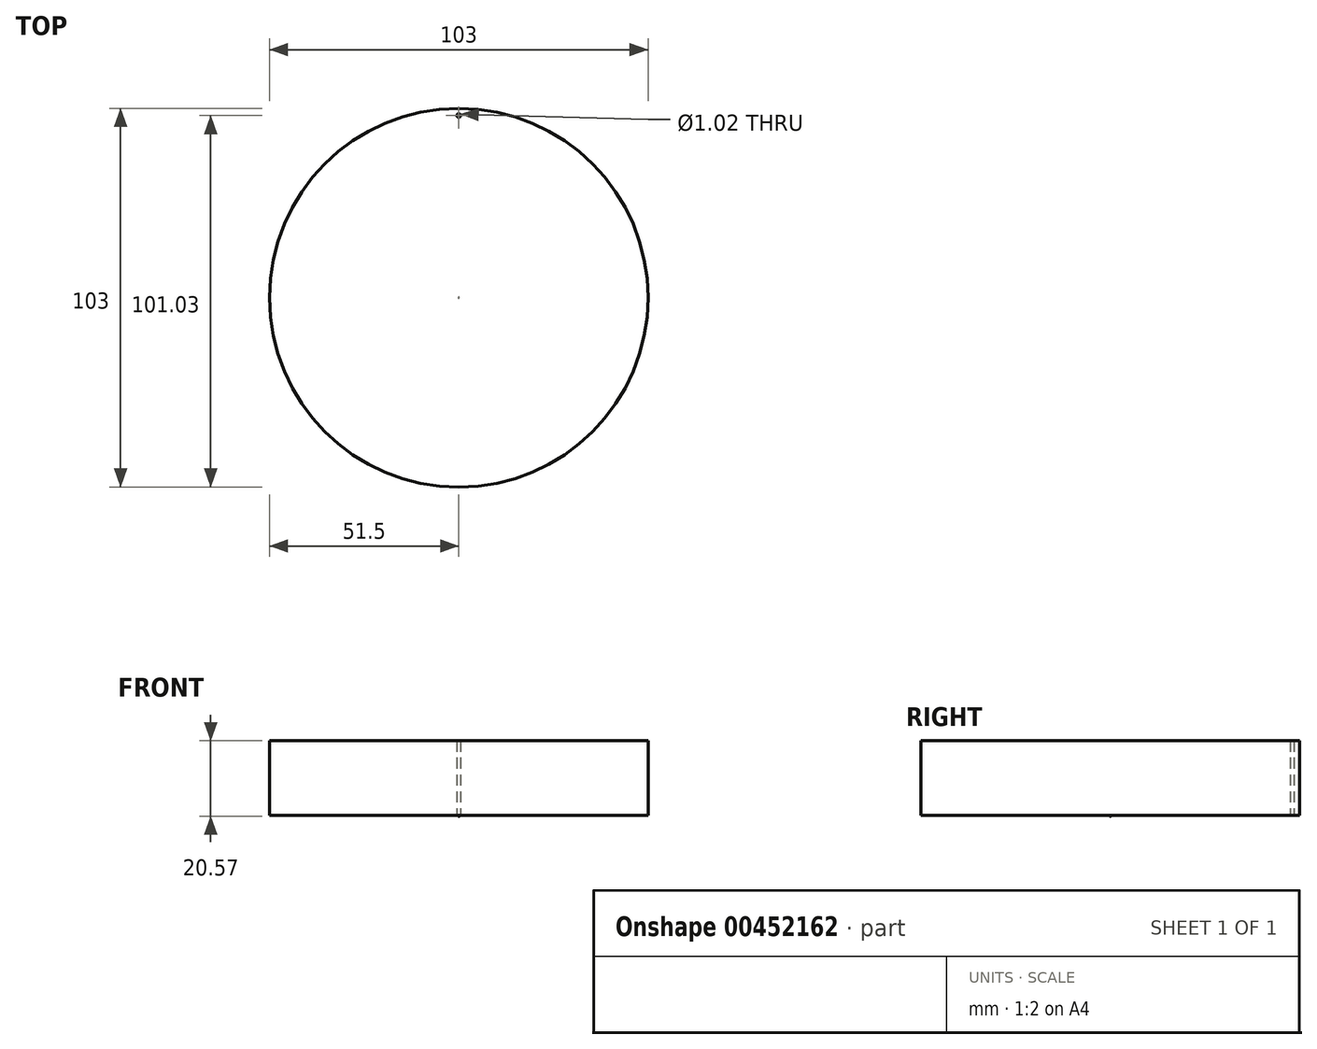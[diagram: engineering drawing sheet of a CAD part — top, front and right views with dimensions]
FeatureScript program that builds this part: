
annotation { "Feature Type Name" : "Feature", "Feature Type Description" : "" }
export const myFeature = defineFeature(function(context is Context, id is Id, definition is map)
    precondition{}
    {
        {
            var Q0;
            Q0=qCreatedBy(makeId("Top.planeOp"),FACE);
            var sketch = newSketch(context, id + "F0", { "sketchPlane" : qUnion([Q0])});
            skCircle(sketch, "E0", {"center": v(0, 0) * mm, "radius": 51.5 * mm});
            skSolve(sketch);
        }
        {
            var Q0;
            Q0=makeQuery(id+"F0.imprint","IMPRINT",FACE,{"disambiguationData":[TD([[makeQuery(id+"F0.imprint","IMPRINT",EDGE,{"derivedFrom":sQuery(id+"F0.wireOp",EDGE,"E0")}),1.0]])]});
            extrude(context, id + "F1", {"entities" : qUnion([Q0]), "depth" : 20.32 * mm});
        }
        {
            var Q0;
            Q0=qCreatedBy(makeId("Top.planeOp"),FACE);
            var sketch = newSketch(context, id + "F2", { "sketchPlane" : qUnion([Q0])});
            skCircle(sketch, "E1", {"center": v(0, 49.53) * mm, "radius": 0.5 * mm});
            skSolve(sketch);
        }
        {
            var Q0;
            Q0=qCreatedBy(makeId("Top.planeOp"),FACE);
            var sketch = newSketch(context, id + "F3", { "sketchPlane" : qUnion([Q0])});
            skCircle(sketch, "E2", {"center": v(0, 0) * mm, "radius": 0.13 * mm});
            skSolve(sketch);
        }
        {
            var Q0;
            Q0 = qSketchRegion(id + "F3", true);
            extrude(context, id + "F4", {"entities" : qUnion([Q0]), "oppositeDirection" : true, "depth" : 0.25 * mm});
        }
        {
            var Q0;
            Q0=makeQuery(id+"F2.imprint","IMPRINT",FACE,{"disambiguationData":[TD([[makeQuery(id+"F2.imprint","IMPRINT",EDGE,{"derivedFrom":sQuery(id+"F2.wireOp",EDGE,"E1")}),1.0]])]});
            extrude(context, id + "F5", {"entities" : qUnion([Q0]), "operationType" : NewBodyOperationType.REMOVE, "depth" : 25.4 * mm});
        }
    });
